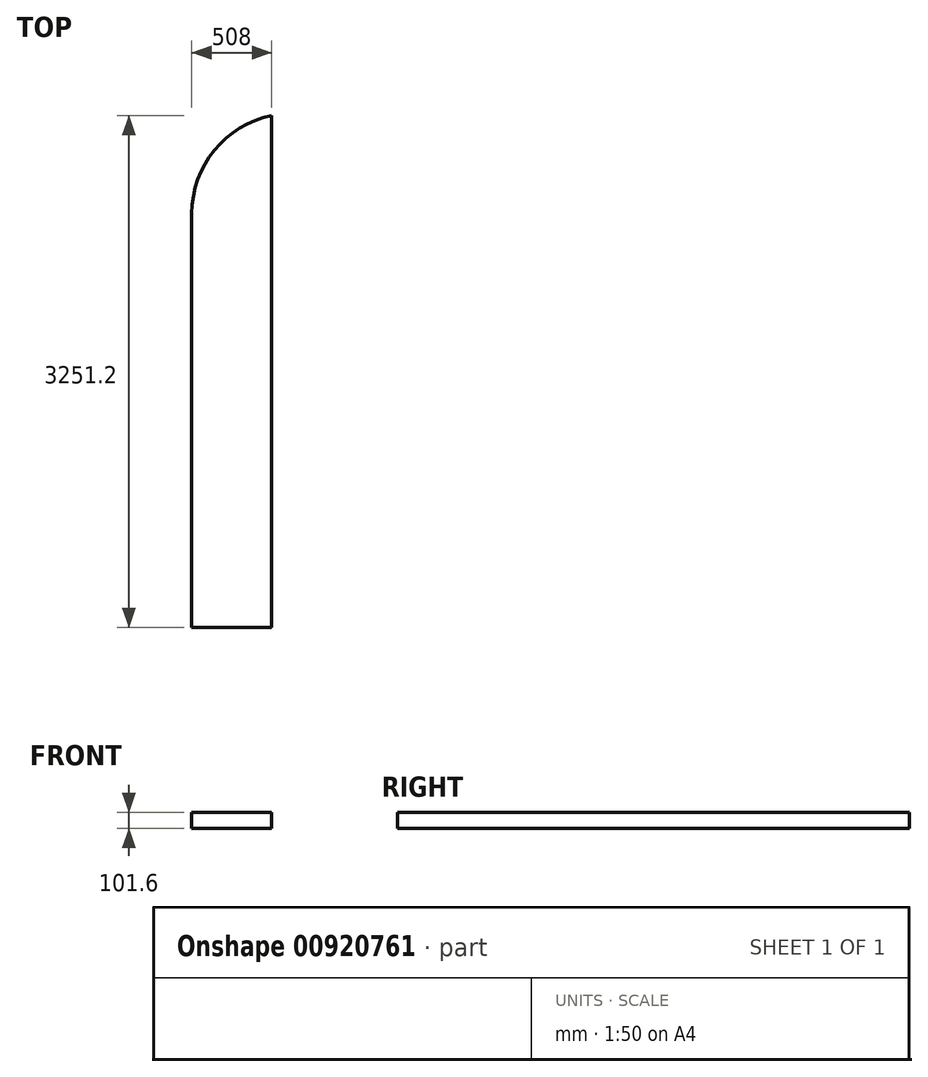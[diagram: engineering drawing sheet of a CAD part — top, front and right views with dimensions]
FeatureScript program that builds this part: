
annotation { "Feature Type Name" : "Feature", "Feature Type Description" : "" }
export const myFeature = defineFeature(function(context is Context, id is Id, definition is map)
    precondition{}
    {
        {
            var Q0;
            Q0=qCreatedBy(makeId("Top.planeOp"),FACE);
            var sketch = newSketch(context, id + "F0", { "sketchPlane" : qUnion([Q0])});
            skLineSegment(sketch, "E0.bottom", {"start": v(254, 1625.6) * mm, "end": v(-254, 1625.6) * mm});
            skLineSegment(sketch, "E0.top", {"start": v(254, -1625.6) * mm, "end": v(-254, -1625.6) * mm});
            skLineSegment(sketch, "E0.left", {"start": v(254, 1625.6) * mm, "end": v(254, -1625.6) * mm});
            skLineSegment(sketch, "E0.right", {"start": v(-254, 1625.6) * mm, "end": v(-254, -1625.6) * mm});
            skPoint(sketch, "E0.middle", {"position": v(0, 0) * mm});
            skSolve(sketch);
        }
        {
            var Q0;
            Q0 = qSketchRegion(id + "F0", true);
            extrude(context, id + "F1", {"entities" : qUnion([Q0]), "depth" : 101.6 * mm, "offsetDistance" : 25.4 * mm});
        }
        {
            var Q0;
            Q0=makeQuery(id+"F1.opExtrude","SWEPT_EDGE",EDGE,{"disambiguationData":[OSD([sQuery(id+"F0.wireOp",EDGE,"E0.bottom"),sQuery(id+"F0.wireOp",EDGE,"E0.right")])]});
            fillet(context, id + "F2", {"entities" : qUnion([Q0]), "radius" : 635 * mm, "tangentPropagation" : true, "allowEdgeOverflow" : false});
        }
    });
